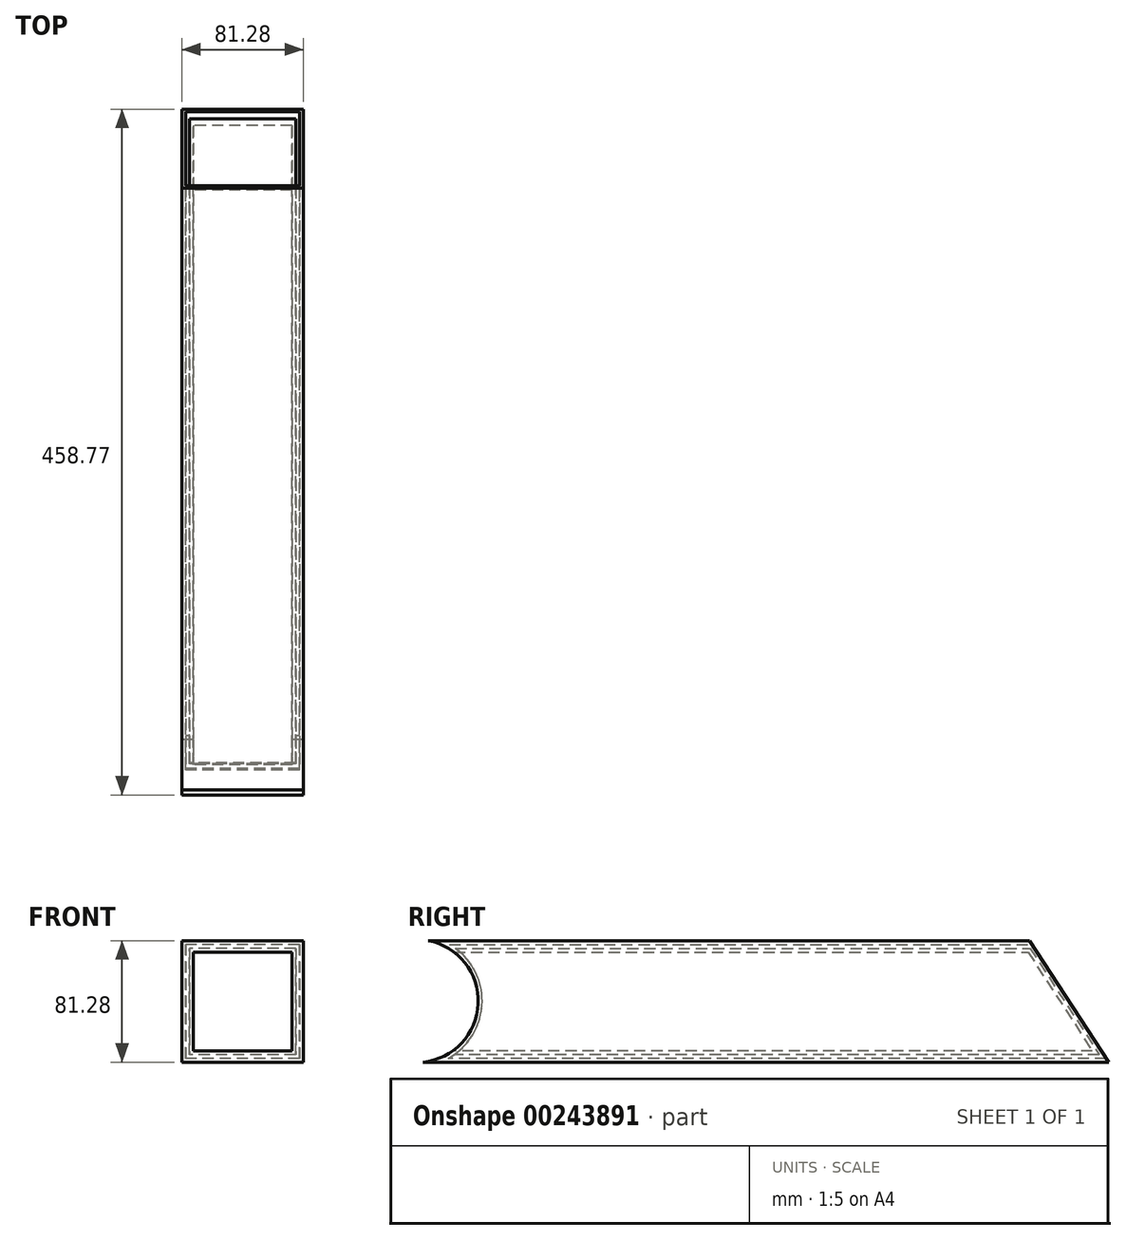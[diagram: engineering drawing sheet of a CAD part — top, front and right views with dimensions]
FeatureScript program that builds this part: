
annotation { "Feature Type Name" : "Feature", "Feature Type Description" : "" }
export const myFeature = defineFeature(function(context is Context, id is Id, definition is map)
    precondition{}
    {
        {
            var Q0;
            Q0=qCreatedBy(makeId("Right.planeOp"),FACE);
            var sketch = newSketch(context, id + "F0", { "sketchPlane" : qUnion([Q0])});
            skLineSegment(sketch, "E0", {"start": v(-112.53, 76.2) * mm, "end": v(277.33, 76.2) * mm});
            skLineSegment(sketch, "E1", {"start": v(277.33, 76.2) * mm, "end": v(326.95, 0) * mm});
            skLineSegment(sketch, "E2", {"start": v(326.95, 0) * mm, "end": v(-113.41, 0) * mm});
            skArc(sketch, "E3", {"start": v(-113.41, 0) * mm, "mid": v(-90.6, 37.84) * mm, "end": v(-112.53, 76.2) * mm});
            skSolve(sketch);
        }
        {
            var Q0;
            Q0=makeQuery(id+"F0.imprint","IMPRINT",FACE,{"disambiguationData":[TD([[makeQuery(id+"F0.imprint","IMPRINT",EDGE,{"derivedFrom":sQuery(id+"F0.wireOp",EDGE,"E0")}),-1.0]])]});
            extrude(context, id + "F1", {"entities" : qUnion([Q0]), "endBound" : BoundingType.SYMMETRIC, "depth" : 76.2 * mm});
        }
        {
            var Q0;
            Q0=makeQuery(id+"F1.opExtrude","SWEPT_FACE",FACE,{"disambiguationData":[OSD([sQuery(id+"F0.wireOp",EDGE,"E3")])]});
            shell(context, id + "F2", {"entities" : qUnion([Q0]), "thickness" : 2.54 * mm});
        }
        {
            var Q0;
            Q0=makeQuery(id+"F1.opExtrude","SWEPT_FACE",FACE,{"disambiguationData":[OSD([sQuery(id+"F0.wireOp",EDGE,"E1")])]});
            shell(context, id + "F3", {"entities" : qUnion([Q0]), "thickness" : 2.54 * mm, "oppositeDirection" : true});
        }
    });
